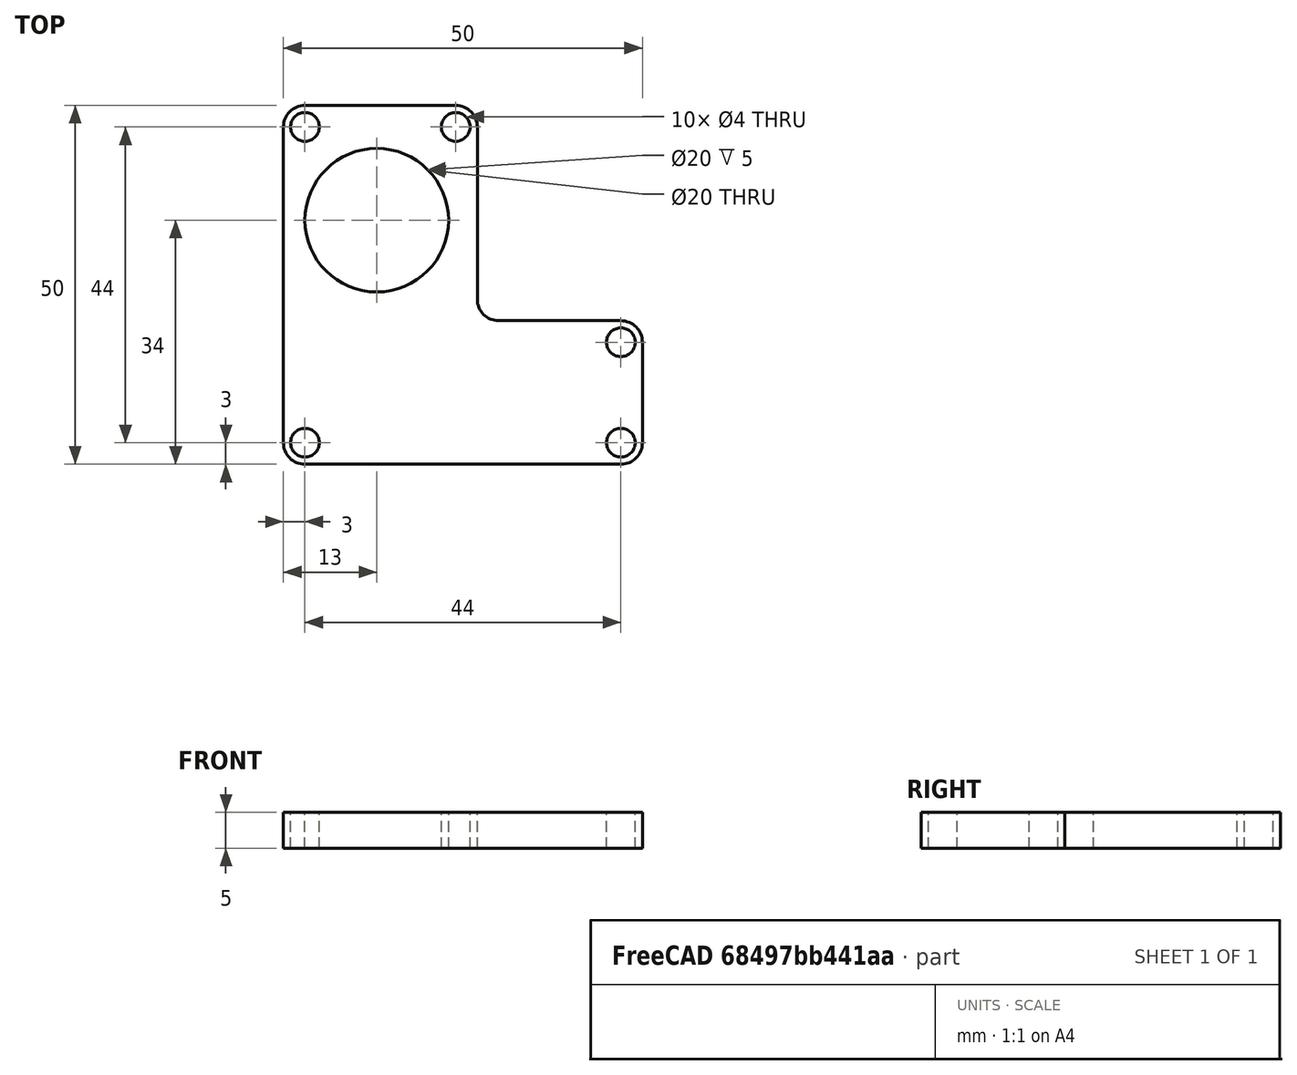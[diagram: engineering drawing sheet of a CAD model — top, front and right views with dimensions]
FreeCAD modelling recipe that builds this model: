
FCSTD DOCUMENT  (FreeCAD 0.17R13541 (Git))
Label: 电机安装板
License: All rights reserved
LicenseURL: http://en.wikipedia.org/wiki/All_rights_reserved
objects: Part::Cylinder×6, Part::Box×2, Part::Fuse×1, Part::MultiFuse×1, Part::Cut×1, Part::Fillet×1, Part::Feature×1
note: 13 computed .brp shape members not serialized (recipe doc carries the construction recipe); baked Part::Feature solids carry a one-line shape summary decoded from their .brp

FEATURE [Part::Box] Box  label="立方体"
  AttacherType = Attacher::AttachEngine3D
  Height = 5
  Length = 27
  Width = 50
FEATURE [Part::Box] Box001  label="立方体001"
  AttacherType = Attacher::AttachEngine3D
  Height = 5
  Length = 50
  Width = 20
FEATURE [Part::Fuse] Fusion
  Base = -> Box
  Tool = -> Box001
FEATURE [Part::Cylinder] Cylinder  label="圆柱体"
  Angle = 360
  AttacherType = Attacher::AttachEngine3D
  Height = 10
  Placement = pos=(47,17,0) rot=(0,0,1;0rad)
  Radius = 2
FEATURE [Part::Cylinder] Cylinder001  label="圆柱体001"
  Angle = 360
  AttacherType = Attacher::AttachEngine3D
  Height = 10
  Placement = pos=(24,47,0) rot=(0,0,1;0rad)
  Radius = 2
FEATURE [Part::Cylinder] Cylinder002  label="圆柱体002"
  Angle = 360
  AttacherType = Attacher::AttachEngine3D
  Height = 10
  Placement = pos=(3,47,0) rot=(0,0,1;0rad)
  Radius = 2
FEATURE [Part::Cylinder] Cylinder003  label="圆柱体003"
  Angle = 360
  AttacherType = Attacher::AttachEngine3D
  Height = 10
  Placement = pos=(13,34,0) rot=(0,0,1;0rad)
  Radius = 10
FEATURE [Part::Cylinder] Cylinder004  label="圆柱体004"
  Angle = 360
  AttacherType = Attacher::AttachEngine3D
  Height = 10
  Placement = pos=(3,3,0) rot=(0,0,1;0rad)
  Radius = 2
FEATURE [Part::Cylinder] Cylinder005  label="圆柱体005"
  Angle = 360
  AttacherType = Attacher::AttachEngine3D
  Height = 10
  Placement = pos=(47,3,0) rot=(0,0,1;0rad)
  Radius = 2
FEATURE [Part::MultiFuse] Fusion001
  Shapes = -> [Cylinder,Cylinder002,Cylinder004,Cylinder001,Cylinder005,Cylinder003]
FEATURE [Part::Cut] Cut
  Base = -> Fusion
  Tool = -> Fusion001
FEATURE [Part::Fillet] Fillet
  Base = -> Cut
  Edges = 6 edges r=3: [Edge2,Edge4,Edge12,Edge27,Edge33,Edge40]
FEATURE [Part::Feature] Fillet001
  shape: bbox 50 x 50 x 5 mm, 20 faces (baked)
